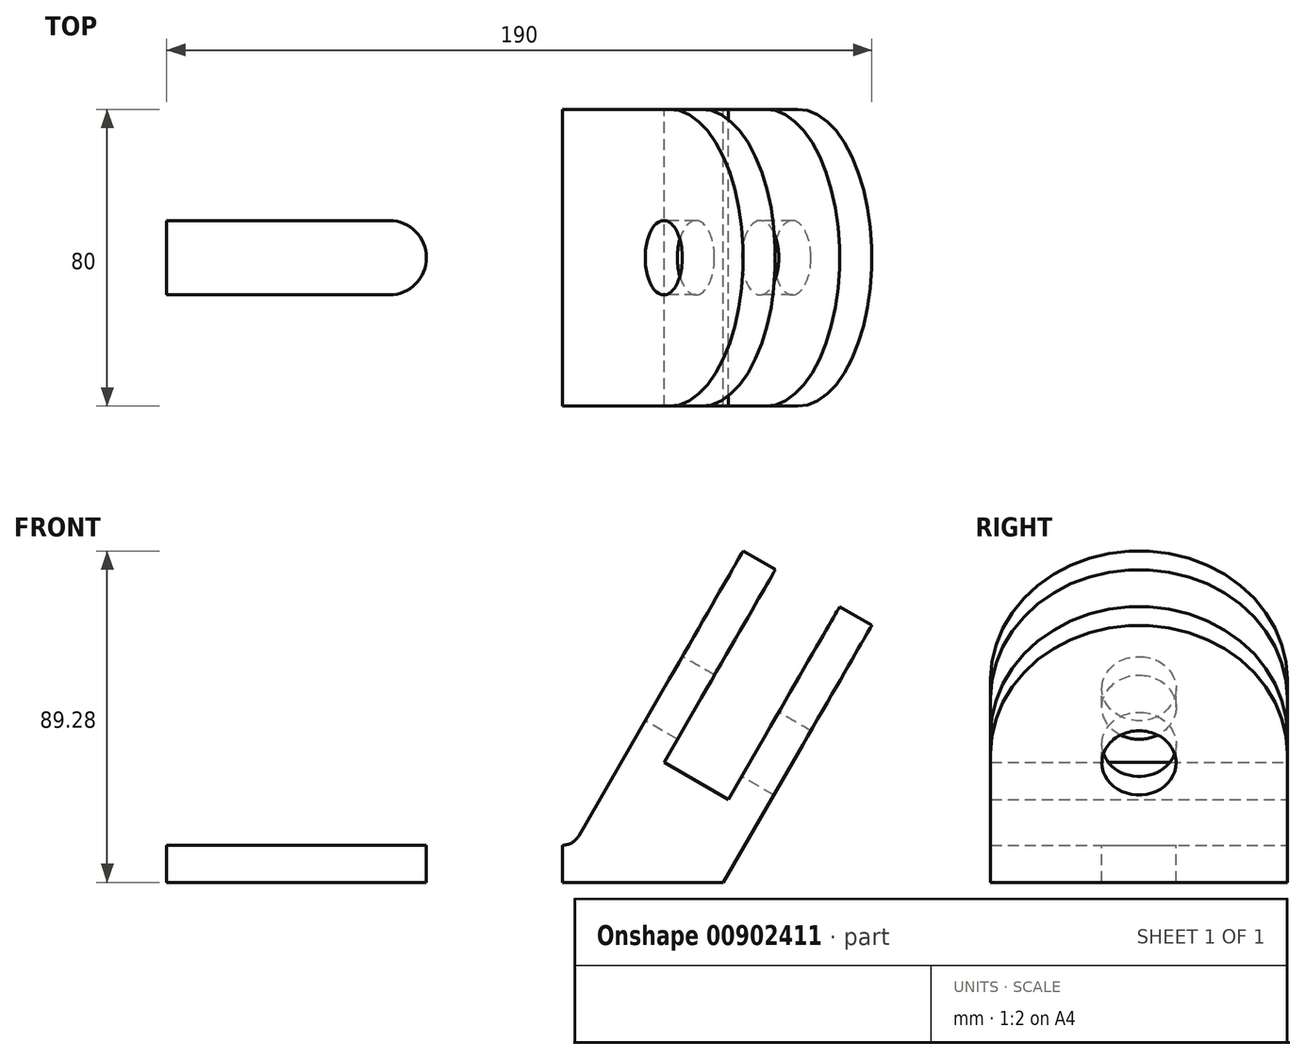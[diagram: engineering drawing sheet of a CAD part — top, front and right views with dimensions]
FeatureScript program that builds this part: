
annotation { "Feature Type Name" : "Feature", "Feature Type Description" : "" }
export const myFeature = defineFeature(function(context is Context, id is Id, definition is map)
    precondition{}
    {
        {
            var Q0;
            Q0=qCreatedBy(makeId("Front.planeOp"),FACE);
            var sketch = newSketch(context, id + "F0", { "sketchPlane" : qUnion([Q0])});
            skLineSegment(sketch, "E0", {"start": v(0, 0) * mm, "end": v(150, 0) * mm});
            skLineSegment(sketch, "E1", {"start": v(150, 0) * mm, "end": v(190, 69.28) * mm});
            skLineSegment(sketch, "E2.0", {"start": v(0, 10) * mm, "end": v(109.59, 10) * mm});
            skLineSegment(sketch, "E3.0", {"start": v(109.59, 10) * mm, "end": v(155.36, 89.28) * mm});
            skLineSegment(sketch, "E4.0", {"start": v(151.34, 22.32) * mm, "end": v(181.34, 74.28) * mm});
            skLineSegment(sketch, "E5.0", {"start": v(134.02, 32.32) * mm, "end": v(164.02, 84.28) * mm});
            skLineSegment(sketch, "E6", {"start": v(0, 10) * mm, "end": v(0, 0) * mm});
            skLineSegment(sketch, "E7", {"start": v(155.36, 89.28) * mm, "end": v(164.02, 84.28) * mm});
            skLineSegment(sketch, "E8", {"start": v(181.34, 74.28) * mm, "end": v(190, 69.28) * mm});
            skLineSegment(sketch, "E9", {"start": v(134.02, 32.32) * mm, "end": v(151.34, 22.32) * mm});
            skSolve(sketch);
        }
        {
            var Q0;
            Q0=makeQuery(id+"F0.imprint","IMPRINT",FACE,{"disambiguationData":[TD([[makeQuery(id+"F0.imprint","IMPRINT",EDGE,{"derivedFrom":sQuery(id+"F0.wireOp",EDGE,"E0")}),1.0]])]});
            extrude(context, id + "F1", {"entities" : qUnion([Q0]), "endBound" : BoundingType.SYMMETRIC, "depth" : 80 * mm, "offsetDistance" : 25 * mm});
        }
        {
            var Q0;
            Q0=makeQuery(id+"F1.opExtrude","CAP_EDGE",EDGE,{"disambiguationData":[OSD([sQuery(id+"F0.wireOp",EDGE,"E7")])],"isStart":false});
            var Q1;
            Q1=makeQuery(id+"F1.opExtrude","CAP_EDGE",EDGE,{"disambiguationData":[OSD([sQuery(id+"F0.wireOp",EDGE,"E7")])],"isStart":true});
            var Q2;
            Q2=makeQuery(id+"F1.opExtrude","CAP_EDGE",EDGE,{"disambiguationData":[OSD([sQuery(id+"F0.wireOp",EDGE,"E8")])],"isStart":true});
            var Q3;
            Q3=makeQuery(id+"F1.opExtrude","CAP_EDGE",EDGE,{"disambiguationData":[OSD([sQuery(id+"F0.wireOp",EDGE,"E8")])],"isStart":false});
            fillet(context, id + "F2", {"entities" : qUnion([Q0, Q1, Q2, Q3]), "radius" : 40 * mm, "tangentPropagation" : true, "allowEdgeOverflow" : false});
        }
        {
            var Q0;
            Q0=makeQuery(id+"F1.opExtrude","CAP_EDGE",EDGE,{"disambiguationData":[OSD([sQuery(id+"F0.wireOp",EDGE,"E6")])],"isStart":false});
            var Q1;
            Q1=makeQuery(id+"F1.opExtrude","CAP_EDGE",EDGE,{"disambiguationData":[OSD([sQuery(id+"F0.wireOp",EDGE,"E6")])],"isStart":true});
            fillet(context, id + "F3", {"entities" : qUnion([Q0, Q1]), "radius" : 20 * mm, "tangentPropagation" : true, "allowEdgeOverflow" : false});
        }
        {
            var Q0;
            Q0=makeQuery(id+"F1.opExtrude","SWEPT_FACE",FACE,{"disambiguationData":[OSD([sQuery(id+"F0.wireOp",EDGE,"E3.0")])]});
            var sketch = newSketch(context, id + "F4", { "sketchPlane" : qUnion([Q0])});
            skPoint(sketch, "E10", {"position": v(0, 112.15) * mm});
            skSolve(sketch);
        }
        {
            var Q0;
            Q0=sQuery(id+"F4.wireOp",VERTEX,"E10");
            var Q1;
            Q1=makeQuery(id+"F1.opExtrude","SWEPT_BODY",BODY,{"disambiguationData":[OSD([sQuery(id+"F0.wireOp",EDGE,"E0"),sQuery(id+"F0.wireOp",EDGE,"E1"),sQuery(id+"F0.wireOp",EDGE,"E2.0"),sQuery(id+"F0.wireOp",EDGE,"E3.0"),sQuery(id+"F0.wireOp",EDGE,"E4.0"),sQuery(id+"F0.wireOp",EDGE,"E5.0"),sQuery(id+"F0.wireOp",EDGE,"E6"),sQuery(id+"F0.wireOp",EDGE,"E7"),sQuery(id+"F0.wireOp",EDGE,"E8"),sQuery(id+"F0.wireOp",EDGE,"E9")])]});
            hole(context, id + "F5", {"style" : HoleStyle.SIMPLE, "endStyle" : HoleEndStyle.THROUGH, "holeDiameter" : 20 * mm, "majorDiameter" : 5 * mm, "isTappedThrough" : true, "tappedDepth" : 12 * mm, "tapClearance" : 3, "locations" : qUnion([Q0]), "scope" : qUnion([Q1])});
        }
        {
            var Q0;
            Q0=makeQuery(id+"F1.opExtrude","SWEPT_EDGE",EDGE,{"disambiguationData":[OSD([sQuery(id+"F0.wireOp",EDGE,"E2.0"),sQuery(id+"F0.wireOp",EDGE,"E3.0")])]});
            fillet(context, id + "F6", {"entities" : qUnion([Q0]), "radius" : 5 * mm, "tangentPropagation" : true, "allowEdgeOverflow" : false});
        }
        {
            var Q0;
            Q0=makeQuery(id+"F1.opExtrude","SWEPT_FACE",FACE,{"disambiguationData":[OSD([sQuery(id+"F0.wireOp",EDGE,"E2.0")])]});
            var sketch = newSketch(context, id + "F7", { "sketchPlane" : qUnion([Q0])});
            skLineSegment(sketch, "E11", {"start": v(0, 0) * mm, "end": v(60, 0) * mm});
            skArc(sketch, "E12.0.startCap", {"start": v(0, -10) * mm, "mid": v(-10, 0) * mm, "end": v(0, 10) * mm});
            skArc(sketch, "E12.0.endCap", {"start": v(60, 10) * mm, "mid": v(70, 0) * mm, "end": v(60, -10) * mm});
            skLineSegment(sketch, "E12.0.left", {"start": v(0, 10) * mm, "end": v(60, 10) * mm});
            skLineSegment(sketch, "E12.0.right", {"start": v(0, -10) * mm, "end": v(60, -10) * mm});
            skSolve(sketch);
        }
        {
            var Q0;
            Q0=makeQuery(id+"F7.imprint","IMPRINT",FACE,{"disambiguationData":[TD([[makeQuery(id+"F7.imprint","IMPRINT",EDGE,{"derivedFrom":sQuery(id+"F7.wireOp",EDGE,"E12.0.endCap")}),-1.0]])]});
            extrude(context, id + "F8", {"entities" : qUnion([Q0]), "operationType" : NewBodyOperationType.REMOVE, "endBound" : BoundingType.THROUGH_ALL, "oppositeDirection" : true, "depth" : 25 * mm, "offsetDistance" : 25 * mm});
        }
    });
